# Revit family: 304_F383_2__
name_source: partatom
category: Pipe Accessories
units: mm (PartAtom-declared; Revit-internal decimal feet)

## family parameters
Always vertical = Yes
Cut with Voids When Loaded = No
Part Type = Valve - Breaks Into
Round Connector Dimension = Use Diameter
Shared = No
Work Plane-Based = No

## types (3) — shared parameters
A = 45.00°
Description = K - Automatic Balancing Valve - Accessible Pre-Set Cartridge
H6 = 35 mm  [stored 0.114829 ft]
H8 = 109 mm
L2D_Min = 3048 mm
L6 = 11 mm  [stored 0.0360892 ft]
Manufacturer = FlowCon
QmdConnectorList = 301;D;302;D
R3 = 6 mm  [stored 0.019685 ft]
R4 = 11 mm  [stored 0.0360892 ft]
R6 = 17 mm
R7 = 27 mm
URL = http://flowcon.com
magiPartTypeId = 304
magiProductFamilyId = F383.2.*
zero-valued in all types: MC_Default_elevation

## per-type parameters (varying)
- F383.2.L.B: CenSd_RN_6=24 mm; CenSd_SW_6=27 mm; D=50 mm; H4=44 mm; H4__ve=-44 mm; H5=96 mm; H5__ve=-96 mm; H7=31 mm; H7__ve=-31 mm; H9=41 mm; H9__ve=-41 mm; L1=32 mm; L1__ve=-32 mm; L2=27 mm; L2D=226 mm; L2__ve=-27 mm; L3=68 mm; L4=70 mm; L5=35 mm  [stored 0.114829 ft]; L7=108 mm; LL=113 mm; R=30 mm  [stored 0.0984252 ft]; R2=34 mm; R5=36 mm; RN=28 mm; SW=31 mm; W2D=50 mm  [stored 0.164042 ft]; magiProductId=F383.2.L
- F383.2.N.B: CenSd_RN_6=38 mm; CenSd_SW_6=43 mm; D=80 mm; H4=38 mm; H4__ve=-38 mm; H5=85 mm; H5__ve=-85 mm; H7=28 mm; H7__ve=-28 mm; H9=65 mm; H9__ve=-65 mm; L1=36 mm; L1__ve=-36 mm; L2=31 mm; L2D=259 mm; L2__ve=-31 mm; L3=78 mm; L4=78 mm; L5=39 mm  [stored 0.127953 ft]; L7=124 mm; LL=130 mm; R=48 mm; R2=54 mm; R5=58 mm; RN=44 mm; SW=50 mm  [stored 0.164042 ft]; W2D=80 mm; magiProductId=F383.2.N
- F383.2.M.B: CenSd_RN_6=31 mm; CenSd_SW_6=35 mm  [stored 0.114829 ft]; D=65 mm; H4=41 mm; H4__ve=-41 mm; H5=90 mm; H5__ve=-90 mm; H7=30 mm  [stored 0.0984252 ft]; H7__ve=-30 mm; H9=53 mm; H9__ve=-53 mm; L1=35 mm  [stored 0.114829 ft]; L1__ve=-35 mm; L2=30 mm  [stored 0.0984252 ft]; L2D=249 mm; L2__ve=-30 mm; L3=75 mm; L4=76 mm; L5=38 mm; L7=120 mm; LL=125 mm; R=39 mm  [stored 0.127953 ft]; R2=44 mm; R5=47 mm; RN=36 mm; SW=41 mm; W2D=65 mm; magiProductId=F383.2.M

note: column(s) folded — value = type name in every type: magiProductCode

note: [stored X ft] marks values corroborated as IEEE doubles in the binary element streams (Revit-internal decimal feet)

## geometry (parser evidence)
native form markers: Sweep x2
no freeform markers — native parametric forms only
